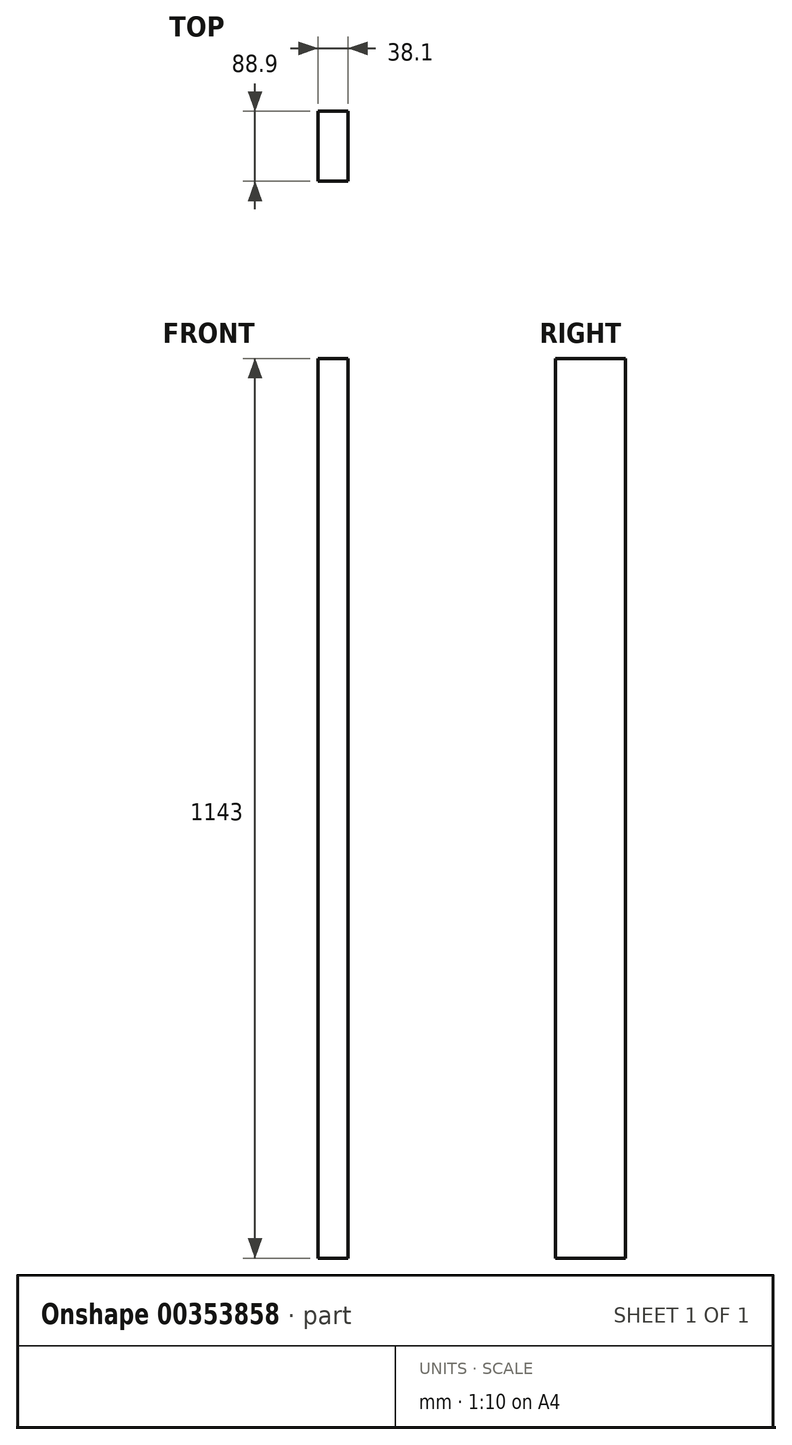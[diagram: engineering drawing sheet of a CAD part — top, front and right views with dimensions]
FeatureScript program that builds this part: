
annotation { "Feature Type Name" : "Feature", "Feature Type Description" : "" }
export const myFeature = defineFeature(function(context is Context, id is Id, definition is map)
    precondition{}
    {
        {
            var Q0;
            Q0=qCreatedBy(makeId("Front.planeOp"),FACE);
            var sketch = newSketch(context, id + "F0", { "sketchPlane" : qUnion([Q0])});
            skLineSegment(sketch, "E0.bottom", {"start": v(-13.4, 1092.23) * mm, "end": v(24.7, 1092.23) * mm});
            skLineSegment(sketch, "E0.top", {"start": v(-13.4, -50.77) * mm, "end": v(24.7, -50.77) * mm});
            skLineSegment(sketch, "E0.left", {"start": v(-13.4, 1092.23) * mm, "end": v(-13.4, -50.77) * mm});
            skLineSegment(sketch, "E0.right", {"start": v(24.7, 1092.23) * mm, "end": v(24.7, -50.77) * mm});
            skSolve(sketch);
        }
        {
            var Q0;
            Q0=makeQuery(id+"F0.imprint","IMPRINT",FACE,{"disambiguationData":[TD([[makeQuery(id+"F0.imprint","IMPRINT",EDGE,{"derivedFrom":sQuery(id+"F0.wireOp",EDGE,"E0.bottom")}),-1.0]])]});
            extrude(context, id + "F1", {"entities" : qUnion([Q0]), "depth" : 88.9 * mm});
        }
    });
